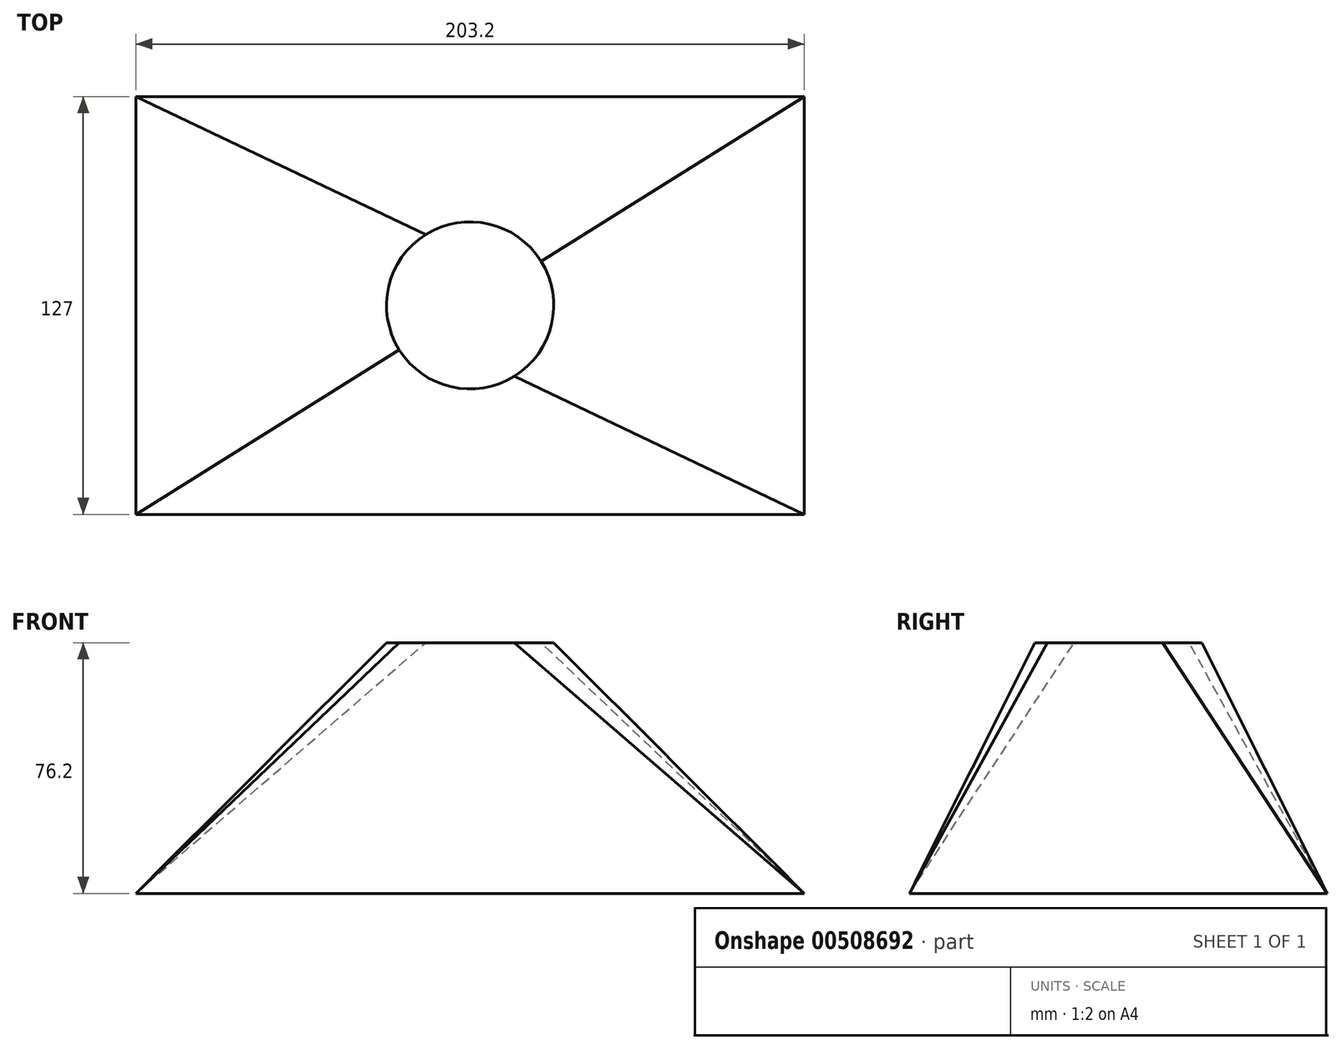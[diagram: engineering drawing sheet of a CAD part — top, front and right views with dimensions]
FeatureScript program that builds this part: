
annotation { "Feature Type Name" : "Feature", "Feature Type Description" : "" }
export const myFeature = defineFeature(function(context is Context, id is Id, definition is map)
    precondition{}
    {
        {
            var Q0;
            Q0=qCreatedBy(makeId("Top.planeOp"),FACE);
            var sketch = newSketch(context, id + "F0", { "sketchPlane" : qUnion([Q0])});
            skLineSegment(sketch, "E0.bottom", {"start": v(101.6, 63.5) * mm, "end": v(-101.6, 63.5) * mm});
            skLineSegment(sketch, "E0.top", {"start": v(101.6, -63.5) * mm, "end": v(-101.6, -63.5) * mm});
            skLineSegment(sketch, "E0.left", {"start": v(101.6, 63.5) * mm, "end": v(101.6, -63.5) * mm});
            skLineSegment(sketch, "E0.right", {"start": v(-101.6, 63.5) * mm, "end": v(-101.6, -63.5) * mm});
            skPoint(sketch, "E0.middle", {"position": v(0, 0) * mm});
            skSolve(sketch);
        }
        {
            var Q0;
            Q0=qCreatedBy(makeId("Top.planeOp"),FACE);
            cPlane(context, id + "F1", {"entities" : qUnion([Q0]), "cplaneType" : CPlaneType.OFFSET, "offset" : 76.2 * mm, "width" : 152.4 * mm, "height" : 152.4 * mm});
        }
        {
            var Q0;
            Q0=qCreatedBy(id+"F1.planeOp",FACE);
            var sketch = newSketch(context, id + "F2", { "sketchPlane" : qUnion([Q0])});
            skCircle(sketch, "E1", {"center": v(0, 0) * mm, "radius": 25.4 * mm});
            skSolve(sketch);
        }
        {
            var Q0;
            Q0=makeQuery(id+"F0.imprint","IMPRINT",FACE,{"disambiguationData":[TD([[makeQuery(id+"F0.imprint","IMPRINT",EDGE,{"derivedFrom":sQuery(id+"F0.wireOp",EDGE,"E0.bottom")}),1.0]])]});
            var Q1;
            Q1=makeQuery(id+"F2.imprint","IMPRINT",FACE,{"disambiguationData":[TD([[makeQuery(id+"F2.imprint","IMPRINT",EDGE,{"derivedFrom":sQuery(id+"F2.wireOp",EDGE,"E1")}),1.0]])]});
            loft(context, id + "F3", {"sheetProfilesArray" : [{ "sheetProfileEntities" : qUnion([Q0]) }, { "sheetProfileEntities" : qUnion([Q1]) }]});
        }
    });
